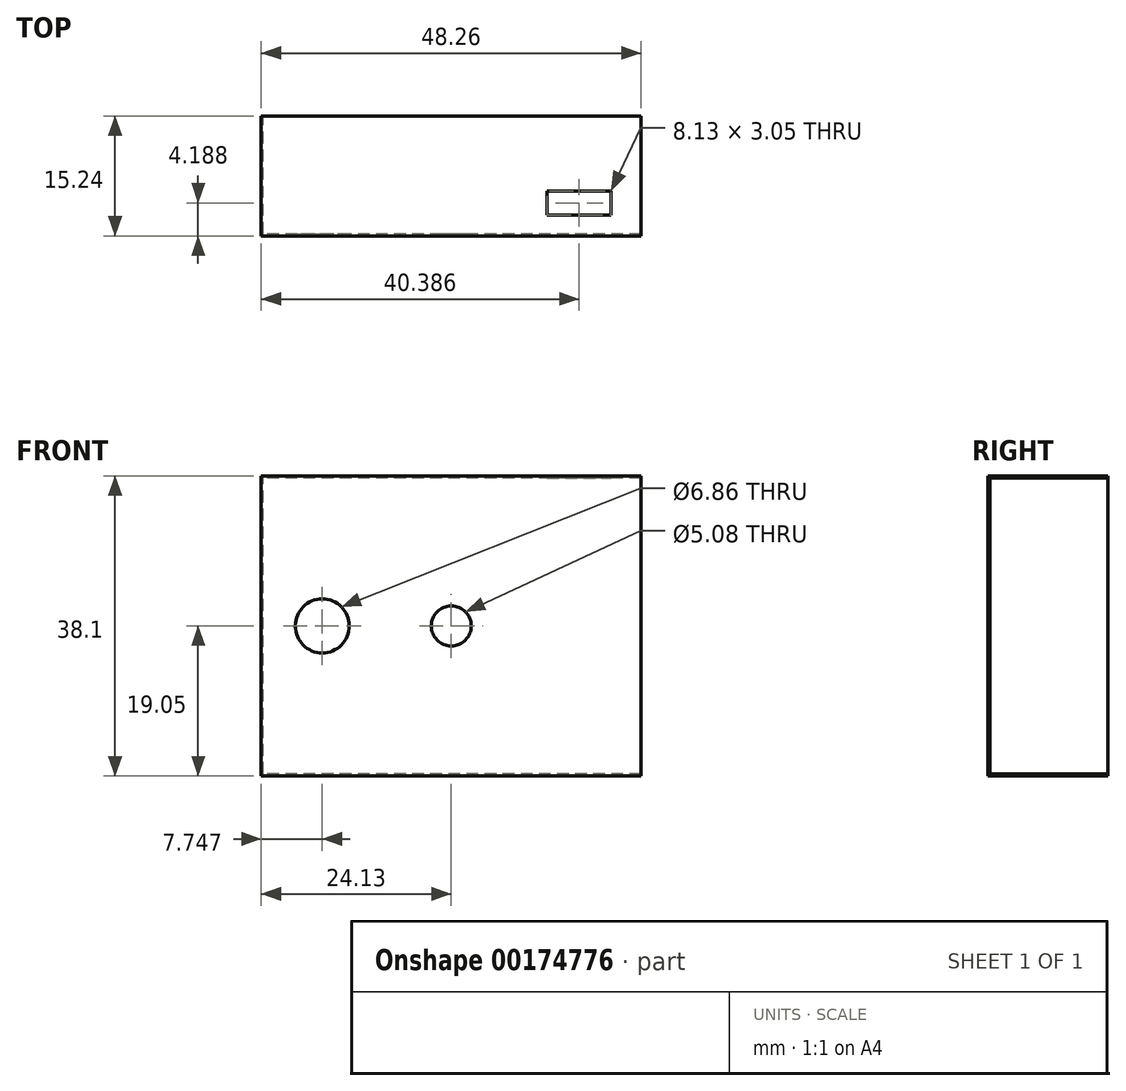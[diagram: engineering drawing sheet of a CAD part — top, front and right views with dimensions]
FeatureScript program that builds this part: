
annotation { "Feature Type Name" : "Feature", "Feature Type Description" : "" }
export const myFeature = defineFeature(function(context is Context, id is Id, definition is map)
    precondition{}
    {
        {
            var Q0;
            Q0=qCreatedBy(makeId("Front.planeOp"),FACE);
            var sketch = newSketch(context, id + "F0", { "sketchPlane" : qUnion([Q0])});
            skLineSegment(sketch, "E0.bottom", {"start": v(24.13, -19.05) * mm, "end": v(-24.13, -19.05) * mm});
            skLineSegment(sketch, "E0.top", {"start": v(24.13, 19.05) * mm, "end": v(-24.13, 19.05) * mm});
            skLineSegment(sketch, "E0.left", {"start": v(24.13, -19.05) * mm, "end": v(24.13, 19.05) * mm});
            skLineSegment(sketch, "E0.right", {"start": v(-24.13, -19.05) * mm, "end": v(-24.13, 19.05) * mm});
            skPoint(sketch, "E0.middle", {"position": v(0, 0) * mm});
            skSolve(sketch);
        }
        {
            var Q0;
            Q0=makeQuery(id+"F0.imprint","IMPRINT",FACE,{"disambiguationData":[TD([[makeQuery(id+"F0.imprint","IMPRINT",EDGE,{"derivedFrom":sQuery(id+"F0.wireOp",EDGE,"E0.bottom")}),-1.0]])]});
            extrude(context, id + "F1", {"entities" : qUnion([Q0]), "depth" : 15.24 * mm});
        }
        {
            var Q0;
            Q0=makeQuery(id+"F1.opExtrude","CAP_FACE",FACE,{"disambiguationData":[OSD([sQuery(id+"F0.wireOp",EDGE,"E0.bottom"),sQuery(id+"F0.wireOp",EDGE,"E0.top"),sQuery(id+"F0.wireOp",EDGE,"E0.left"),sQuery(id+"F0.wireOp",EDGE,"E0.right")])],"isStart":false});
            var sketch = newSketch(context, id + "F2", { "sketchPlane" : qUnion([Q0])});
            skLineSegment(sketch, "E1", {"start": v(-24.13, 2.53) * mm, "end": v(-19.81, 2.53) * mm});
            skLineSegment(sketch, "E2", {"start": v(-24.13, 0) * mm, "end": v(-16.38, 0) * mm});
            skPoint(sketch, "E2.endSnap0", {"position": v(-24.13, 0) * mm});
            skPoint(sketch, "E3.middle", {"position": v(-16.38, 0) * mm});
            skCircle(sketch, "E4", {"center": v(-16.38, 0) * mm, "radius": 3.43 * mm});
            skSolve(sketch);
        }
        {
            var Q0;
            Q0=makeQuery(id+"F1.opExtrude","CAP_FACE",FACE,{"disambiguationData":[OSD([sQuery(id+"F0.wireOp",EDGE,"E0.bottom"),sQuery(id+"F0.wireOp",EDGE,"E0.top"),sQuery(id+"F0.wireOp",EDGE,"E0.left"),sQuery(id+"F0.wireOp",EDGE,"E0.right")])],"isStart":true});
            var Q1;
            Q1=makeQuery(id+"F1.opExtrude","SWEPT_FACE",FACE,{"disambiguationData":[OSD([sQuery(id+"F0.wireOp",EDGE,"E0.left")])]});
            shell(context, id + "F3", {"entities" : qUnion([Q0, Q1]), "thickness" : 0.25 * mm});
        }
        {
            var Q0;
            Q0=sQuery(id+"F2.wireOp",VERTEX,"E3.middle");
            var Q1;
            Q1=makeQuery(id+"F1.opExtrude","SWEPT_BODY",BODY,{"disambiguationData":[OSD([sQuery(id+"F0.wireOp",EDGE,"E0.bottom"),sQuery(id+"F0.wireOp",EDGE,"E0.top"),sQuery(id+"F0.wireOp",EDGE,"E0.left"),sQuery(id+"F0.wireOp",EDGE,"E0.right")])]});
            hole(context, id + "F4", {"style" : HoleStyle.SIMPLE, "endStyle" : HoleEndStyle.THROUGH, "holeDiameter" : 6.86 * mm, "locations" : qUnion([Q0]), "scope" : qUnion([Q1]), "isTappedThrough" : true});
        }
        {
            var Q0;
            Q0=makeQuery(id+"F1.opExtrude","CAP_FACE",FACE,{"disambiguationData":[OSD([sQuery(id+"F0.wireOp",EDGE,"E0.bottom"),sQuery(id+"F0.wireOp",EDGE,"E0.top"),sQuery(id+"F0.wireOp",EDGE,"E0.left"),sQuery(id+"F0.wireOp",EDGE,"E0.right")])],"isStart":false});
            var sketch = newSketch(context, id + "F5", { "sketchPlane" : qUnion([Q0])});
            skCircle(sketch, "E5", {"center": v(0, 0) * mm, "radius": 2.54 * mm});
            skSolve(sketch);
        }
        {
            var Q0;
            Q0=sQuery(id+"F5.wireOp",VERTEX,"E5.center");
            var Q1;
            Q1=makeQuery(id+"F1.opExtrude","SWEPT_BODY",BODY,{"disambiguationData":[OSD([sQuery(id+"F0.wireOp",EDGE,"E0.bottom"),sQuery(id+"F0.wireOp",EDGE,"E0.top"),sQuery(id+"F0.wireOp",EDGE,"E0.left"),sQuery(id+"F0.wireOp",EDGE,"E0.right")])]});
            hole(context, id + "F6", {"style" : HoleStyle.SIMPLE, "endStyle" : HoleEndStyle.THROUGH, "holeDiameter" : 5.08 * mm, "locations" : qUnion([Q0]), "scope" : qUnion([Q1]), "isTappedThrough" : true});
        }
        {
            var Q0;
            Q0=makeQuery(id+"F1.opExtrude","SWEPT_FACE",FACE,{"disambiguationData":[OSD([sQuery(id+"F0.wireOp",EDGE,"E0.top")])]});
            var sketch = newSketch(context, id + "F7", { "sketchPlane" : qUnion([Q0])});
            skLineSegment(sketch, "E6", {"start": v(24.13, -15.24) * mm, "end": v(20.32, -15.24) * mm});
            skLineSegment(sketch, "E7", {"start": v(24.13, -15.24) * mm, "end": v(24.13, -13.2) * mm});
            skLineSegment(sketch, "E8", {"start": v(20.32, -15.24) * mm, "end": v(20.32, -13.2) * mm});
            skLineSegment(sketch, "E9", {"start": v(20.32, -15.24) * mm, "end": v(12.2, -15.24) * mm});
            skLineSegment(sketch, "E10", {"start": v(24.13, -13.2) * mm, "end": v(24.13, -10.16) * mm});
            skLineSegment(sketch, "E11.bottom", {"start": v(20.32, -12.58) * mm, "end": v(12.2, -12.58) * mm});
            skLineSegment(sketch, "E11.top", {"start": v(20.32, -9.53) * mm, "end": v(12.2, -9.53) * mm});
            skLineSegment(sketch, "E11.left", {"start": v(20.32, -12.58) * mm, "end": v(20.32, -9.53) * mm});
            skLineSegment(sketch, "E11.right", {"start": v(12.2, -12.58) * mm, "end": v(12.2, -9.53) * mm});
            skSolve(sketch);
        }
        {
            var Q0;
            Q0=makeQuery(id+"F7.imprint","IMPRINT",FACE,{"disambiguationData":[TD([[makeQuery(id+"F7.imprint","IMPRINT",EDGE,{"derivedFrom":sQuery(id+"F7.wireOp",EDGE,"E11.bottom")}),-1.0]])]});
            extrude(context, id + "F8", {"entities" : qUnion([Q0]), "operationType" : NewBodyOperationType.REMOVE, "oppositeDirection" : true, "depth" : 25.4 * mm});
        }
    });
